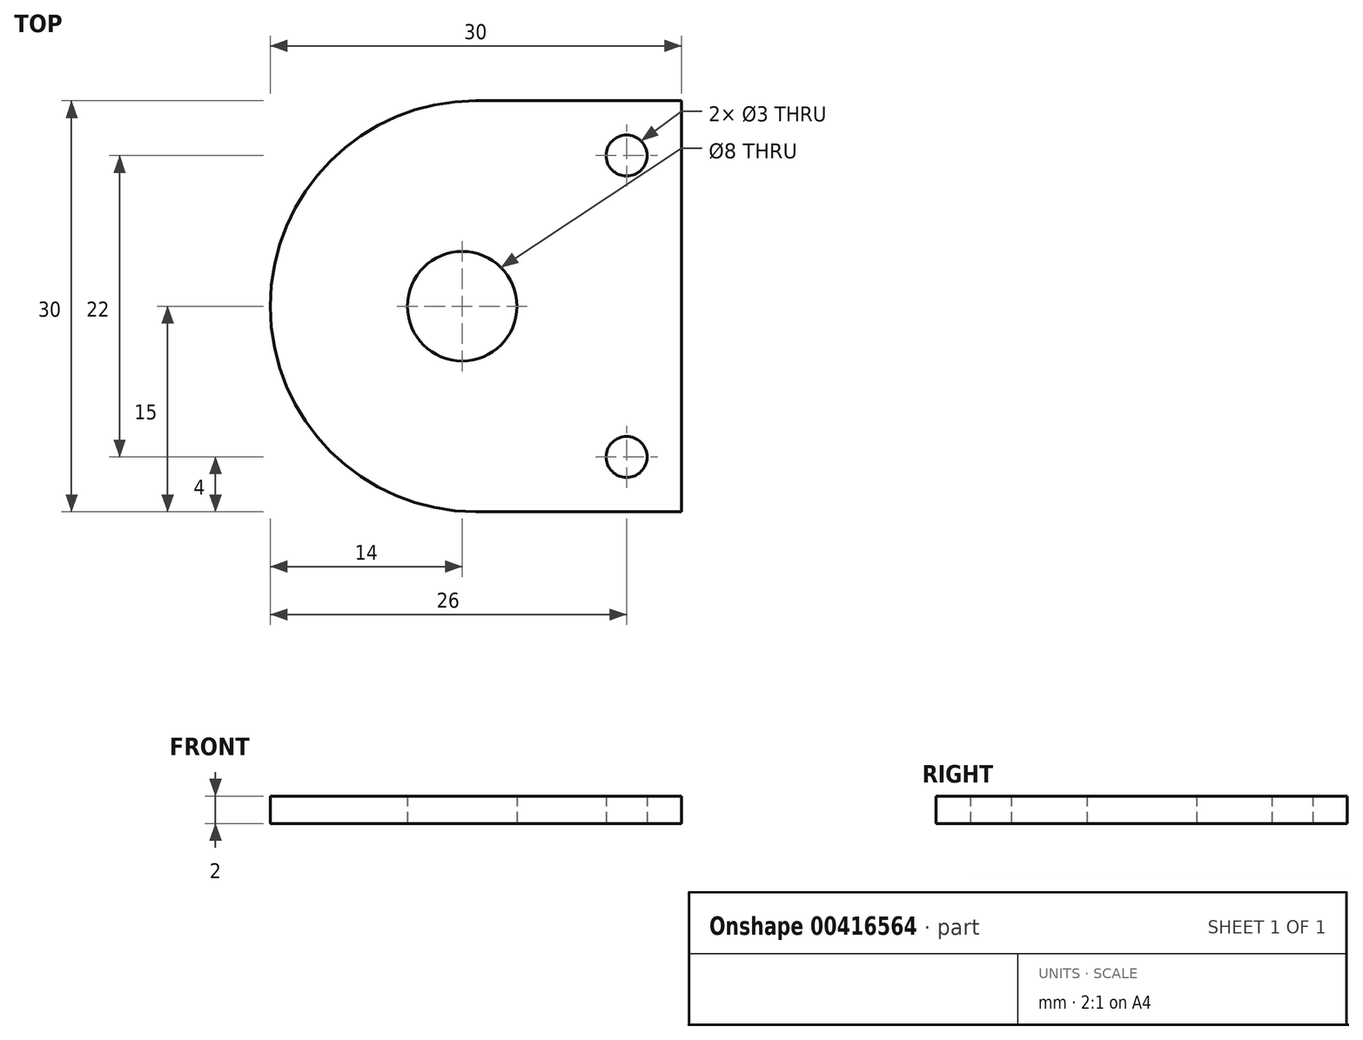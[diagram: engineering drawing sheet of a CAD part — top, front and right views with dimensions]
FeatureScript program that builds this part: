
annotation { "Feature Type Name" : "Feature", "Feature Type Description" : "" }
export const myFeature = defineFeature(function(context is Context, id is Id, definition is map)
    precondition{}
    {
        {
            var Q0;
            Q0=qCreatedBy(makeId("Top.planeOp"),FACE);
            var sketch = newSketch(context, id + "F0", { "sketchPlane" : qUnion([Q0])});
            skLineSegment(sketch, "E0.bottom", {"start": v(0, 0) * mm, "end": v(-30, 0) * mm});
            skLineSegment(sketch, "E0.top", {"start": v(0, 30) * mm, "end": v(-30, 30) * mm});
            skLineSegment(sketch, "E0.left", {"start": v(0, 0) * mm, "end": v(0, 30) * mm});
            skLineSegment(sketch, "E0.right", {"start": v(-30, 0) * mm, "end": v(-30, 30) * mm});
            skCircle(sketch, "E1", {"center": v(-4, 26) * mm, "radius": 1.5 * mm});
            skCircle(sketch, "E2", {"center": v(-4, 4) * mm, "radius": 1.5 * mm});
            skCircle(sketch, "E3", {"center": v(-16, 15) * mm, "radius": 4 * mm});
            skSolve(sketch);
        }
        {
            var Q0;
            Q0=makeQuery(id+"F0.imprint","IMPRINT",FACE,{"disambiguationData":[TD([[makeQuery(id+"F0.imprint","IMPRINT",EDGE,{"derivedFrom":sQuery(id+"F0.wireOp",EDGE,"E0.bottom")}),-1.0]])]});
            extrude(context, id + "F1", {"entities" : qUnion([Q0]), "depth" : 2 * mm, "offsetDistance" : 25 * mm});
        }
        {
            var Q0;
            Q0=makeQuery(id+"F1.opExtrude","SWEPT_EDGE",EDGE,{"disambiguationData":[OSD([sQuery(id+"F0.wireOp",EDGE,"E0.bottom"),sQuery(id+"F0.wireOp",EDGE,"E0.right")])]});
            var Q1;
            Q1=makeQuery(id+"F1.opExtrude","SWEPT_EDGE",EDGE,{"disambiguationData":[OSD([sQuery(id+"F0.wireOp",EDGE,"E0.top"),sQuery(id+"F0.wireOp",EDGE,"E0.right")])]});
            fillet(context, id + "F2", {"entities" : qUnion([Q0, Q1]), "radius" : 15 * mm, "tangentPropagation" : true, "allowEdgeOverflow" : false});
        }
    });
